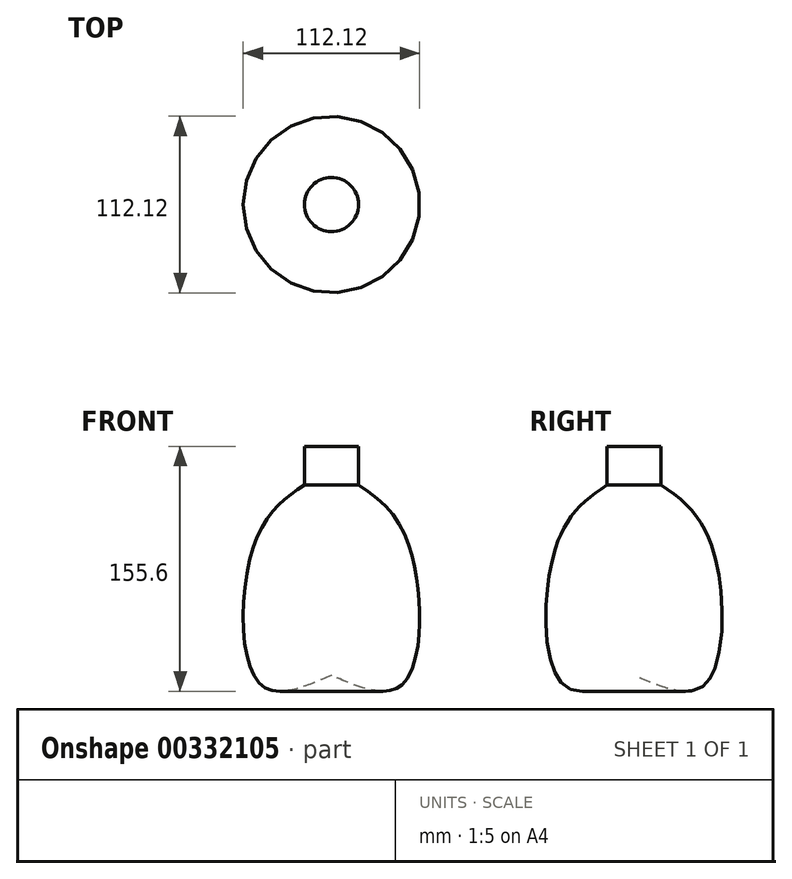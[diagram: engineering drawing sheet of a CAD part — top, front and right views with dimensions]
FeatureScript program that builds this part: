
annotation { "Feature Type Name" : "Feature", "Feature Type Description" : "" }
export const myFeature = defineFeature(function(context is Context, id is Id, definition is map)
    precondition{}
    {
        {
            var Q0;
            Q0=qCreatedBy(makeId("Front.planeOp"),FACE);
            var sketch = newSketch(context, id + "F0", { "sketchPlane" : qUnion([Q0])});
            skLineSegment(sketch, "E0", {"start": v(0, 115.78) * mm, "end": v(0, -100.74) * mm, "construction": true});
            skSolve(sketch);
        }
        {
            var Q0;
            Q0=qCreatedBy(makeId("Front.planeOp"),FACE);
            var sketch = newSketch(context, id + "F1", { "sketchPlane" : qUnion([Q0])});
            skFitSpline(sketch, "E1", {"points": [v(0, -56.06) * mm, v(-45.54, -61.22) * mm, v(-48.54, 28.57) * mm, v(-17.18, 65.08) * mm], "startDerivative": vector(-182.4, -78.04) * mm, "endDerivative": vector(120.68, 83.54) * mm});
            skLineSegment(sketch, "E2", {"start": v(-17.18, 65.08) * mm, "end": v(-17.18, 89.57) * mm});
            skLineSegment(sketch, "E3", {"start": v(-17.18, 89.57) * mm, "end": v(0, 89.57) * mm});
            skLineSegment(sketch, "E4", {"start": v(0, 89.57) * mm, "end": v(0, -56.06) * mm});
            skSolve(sketch);
        }
        {
            var Q0;
            Q0=makeQuery(id+"F1.imprint","IMPRINT",FACE,{"disambiguationData":[TD([[makeQuery(id+"F1.imprint","IMPRINT",EDGE,{"derivedFrom":sQuery(id+"F1.wireOp",EDGE,"E1")}),-1.0]])]});
            var Q1;
            Q1=sQuery(id+"F0.wireOp",EDGE,"E0");
            revolve(context, id + "F2", {"entities" : qUnion([Q0]), "axis" : qUnion([Q1]), "revolveType" : RevolveType.FULL});
        }
    });
